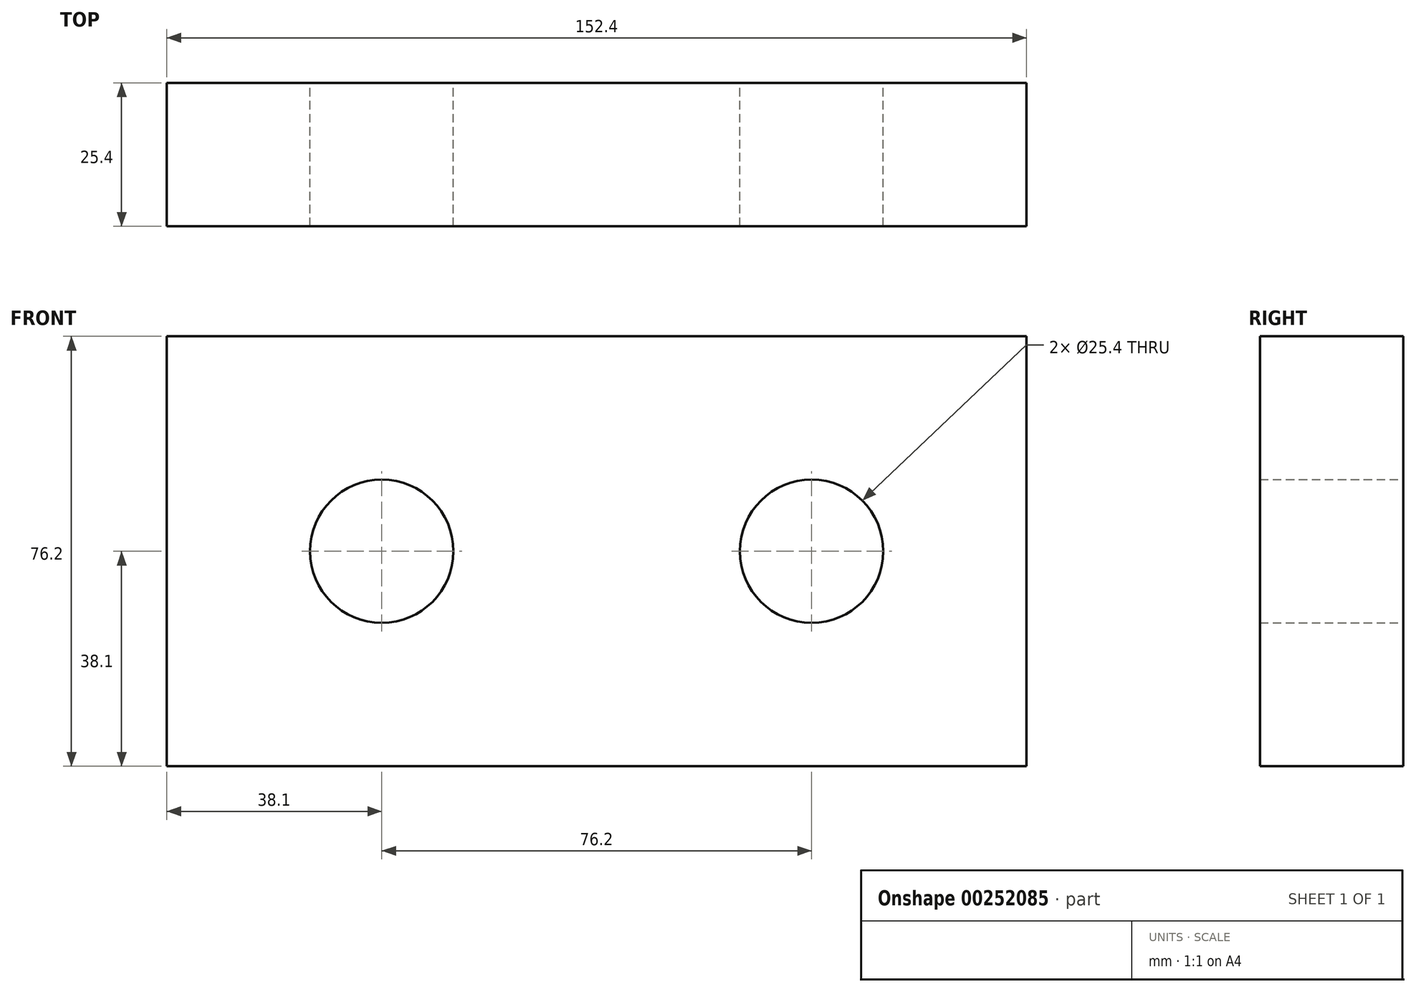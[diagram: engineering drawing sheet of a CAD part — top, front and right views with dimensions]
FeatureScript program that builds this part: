
annotation { "Feature Type Name" : "Feature", "Feature Type Description" : "" }
export const myFeature = defineFeature(function(context is Context, id is Id, definition is map)
    precondition{}
    {
        {
            var Q0;
            Q0=qCreatedBy(makeId("Front.planeOp"),FACE);
            var sketch = newSketch(context, id + "F0", { "sketchPlane" : qUnion([Q0])});
            skLineSegment(sketch, "E0.bottom", {"start": v(76.2, 38.1) * mm, "end": v(-76.2, 38.1) * mm});
            skLineSegment(sketch, "E0.top", {"start": v(76.2, -38.1) * mm, "end": v(-76.2, -38.1) * mm});
            skLineSegment(sketch, "E0.left", {"start": v(76.2, 38.1) * mm, "end": v(76.2, -38.1) * mm});
            skLineSegment(sketch, "E0.right", {"start": v(-76.2, 38.1) * mm, "end": v(-76.2, -38.1) * mm});
            skPoint(sketch, "E0.middle", {"position": v(0, 0) * mm});
            skCircle(sketch, "E1", {"center": v(-38.1, 0) * mm, "radius": 12.7 * mm});
            skCircle(sketch, "E2", {"center": v(38.1, 0) * mm, "radius": 12.7 * mm});
            skSolve(sketch);
        }
        {
            var Q0;
            Q0 = qSketchRegion(id + "F0", true);
            extrude(context, id + "F1", {"entities" : qUnion([Q0]), "depth" : 25.4 * mm});
        }
    });
